# Revit family: Reflex_H_R
name_source: partatom
category: Mechanical Equipment
revit_build: Autodesk Revit 2014 (Build: 20130308_1515(x64)
units: mm (PartAtom-declared; Revit-internal decimal feet)

## types (9) — shared parameters
A1 = 28 mm  [stored 0.0918635 ft]
Angle = 40.00°
Angle1 = 60.00°
Color = gray
Description = Membrane pressure expansion vessel
ETIM Article Class = EC010958
ETIM Name = Membrane pressure expansion vessel
IFCExportAs = ifcexpansion
IFCExportType = EXPANSION
Manufacturer = Reflex
Model = Storatherm Heat H…/R
Reflex_item_color = Color RGB 128-128-128
Revision = 2016
URL = http://reflex.cadprofi.com
V_cov = No

## per-type parameters (varying)
- Reflex H 300/R: A=48.3 mm  [stored 0.158465 ft]; Ang2=0.00°; Art. No.=7783600; Connection=9*Rp 1 1/2; D=597 mm; DL=279.5 mm; DN=40 mm; F=142 mm; H=1320 mm; H1=42 mm; H2=1178 mm; H4=149.25 mm; HC1=225 mm; HC2=490 mm; HC3=760 mm; HC4=1033 mm; HC5=210 mm; HC6=380 mm; HC7=670 mm; HC8=960 mm; HL=750 mm; HRev=265 mm  [stored 0.869423 ft]; HT=0 mm  [stored 0 ft]; LM=398.5 mm; PN=3 bar; RLG=260 mm; RN=520 mm; RT=0 mm  [stored 0 ft]; Scale=1 mm  [stored 0.00328084 ft]; VCon=No; VLeg_b=No; VLeg_m=No; VLeg_s=Yes; VTrans=No; Volume=300.0 L
- Reflex H 500/R: A=48.3 mm  [stored 0.158465 ft]; Ang2=0.00°; Art. No.=7783800; Connection=9*Rp 1 1/2; D=597 mm; DL=279.5 mm; DN=40 mm; F=142 mm; H=1950 mm; H1=42 mm; H2=1808 mm; H4=149.25 mm; HC1=225 mm; HC2=701 mm; HC3=1181 mm; HC4=1655 mm; HC5=210 mm; HC6=375 mm  [stored 1.23031 ft]; HC7=945 mm; HC8=1515 mm; HL=1102 mm; HRev=265 mm  [stored 0.869423 ft]; HT=0 mm  [stored 0 ft]; LM=398.5 mm; PN=3 bar; RLG=260 mm; RN=520 mm; RT=0 mm  [stored 0 ft]; Scale=1 mm  [stored 0.00328084 ft]; VCon=No; VLeg_b=No; VLeg_m=No; VLeg_s=Yes; VTrans=No; Volume=500.0 L
- Reflex H 800/R: A=48.3 mm  [stored 0.158465 ft]; Ang2=0.00°; Art. No.=7784005; Connection=9*Rp 1 1/2; D=790 mm; DL=376 mm; DN=40 mm; F=140 mm; H=1825 mm; H1=40 mm  [stored 0.131234 ft]; H2=1685 mm; H4=197.5 mm  [stored 0.647966 ft]; HC1=236 mm; HC2=656 mm; HC3=1076 mm; HC4=1496 mm; HC5=221 mm; HC6=386 mm  [stored 1.2664 ft]; HC7=896 mm; HC8=1446 mm; HL=1350 mm; HRev=311 mm; HT=0 mm  [stored 0 ft]; LM=495 mm; PN=3 bar; RLG=345.5 mm  [stored 1.13353 ft]; RN=691 mm; RT=0 mm  [stored 0 ft]; Scale=1 mm  [stored 0.00328084 ft]; VCon=No; VLeg_b=No; VLeg_m=Yes; VLeg_s=No; VTrans=No; Volume=800.0 L
- Reflex H 1000/R: A=48.3 mm  [stored 0.158465 ft]; Ang2=0.00°; Art. No.=7784205; Connection=9*Rp 1 1/2; D=790 mm; DL=366.5 mm; DN=40 mm; F=180 mm  [stored 0.590551 ft]; H=2115 mm; H1=80 mm  [stored 0.262467 ft]; H2=1898 mm; H4=197.5 mm  [stored 0.647966 ft]; HC1=310 mm  [stored 1.01706 ft]; HC2=768 mm; HC3=1228 mm; HC4=1681 mm; HC5=296 mm  [stored 0.971129 ft]; HC6=461 mm; HC7=1011 mm; HC8=1581 mm; HL=1320 mm; HRev=386 mm  [stored 1.2664 ft]; HT=0 mm  [stored 0 ft]; LM=495 mm; PN=3 bar; RLG=345.5 mm  [stored 1.13353 ft]; RN=691 mm; RT=0 mm  [stored 0 ft]; Scale=1.5 mm  [stored 0.00492126 ft]; VCon=No; VLeg_b=No; VLeg_m=Yes; VLeg_s=No; VTrans=No; Volume=1000.0 L
- Reflex H 1500/R: A=48.3 mm  [stored 0.158465 ft]; Ang2=0.00°; Art. No.=7784400; Connection=9*Rp 1 1/2; D=1000 mm; DL=471.5 mm; DN=40 mm; F=146 mm; H=2120 mm; H1=46 mm; H2=1974 mm; H4=250 mm; HC1=341 mm; HC2=798 mm; HC3=1258 mm; HC4=1716 mm; HC5=341 mm; HC6=551 mm; HC7=1096 mm; HC8=1566 mm; HL=1250 mm; HRev=421 mm; HT=0 mm  [stored 0 ft]; LM=600 mm; PN=6 bar; RLG=437.5 mm; RN=875 mm; RT=0 mm  [stored 0 ft]; Scale=1.5 mm  [stored 0.00492126 ft]; VCon=No; VLeg_b=No; VLeg_m=Yes; VLeg_s=No; VTrans=No; Volume=1500.0 L
- Reflex H 2000/R: A=48.3 mm  [stored 0.158465 ft]; Ang2=0.00°; Art. No.=7784600; Connection=9*Rp 1 1/2; D=1200 mm; DL=571.5 mm; DN=40 mm; F=132 mm; H=2122 mm; H1=32 mm; H2=1990 mm; H4=300 mm; HC1=365 mm; HC2=805 mm; HC3=1245 mm; HC4=1680 mm; HC5=365 mm; HC6=575 mm; HC7=1100 mm; HC8=1630 mm; HL=1500 mm; HRev=421 mm; HT=0 mm  [stored 0 ft]; LM=700 mm; PN=6 bar; RLG=510 mm; RN=1020 mm; RT=0 mm  [stored 0 ft]; Scale=1.5 mm  [stored 0.00492126 ft]; VCon=No; VLeg_b=No; VLeg_m=Yes; VLeg_s=No; VTrans=No; Volume=2000.0 L
- Reflex H 3000/R: A=60.3 mm; Ang2=30.00°; Art. No.=7788200; Connection=9*Rp 2; D=1500 mm; DL=721.5 mm; DN=40 mm; F=191 mm; H=2101 mm; H1=91 mm; H2=1910 mm; H4=375 mm  [stored 1.23031 ft]; HC1=495 mm; HC2=845 mm; HC3=1247 mm; HC4=1597 mm; HC5=495 mm; HC6=845 mm; HC7=1247 mm; HC8=1597 mm; HL=1500 mm; HRev=550 mm; HT=1840 mm; LM=850 mm; PN=6 bar; RLG=550 mm; RN=1100 mm; RT=1320 mm; Scale=1.5 mm  [stored 0.00492126 ft]; VCon=Yes; VLeg_b=Yes; VLeg_m=No; VLeg_s=No; VTrans=Yes; Volume=3000.0 L
- Reflex H 4000/R: A=60.3 mm; Ang2=30.00°; Art. No.=7788500; Connection=9*Rp 2; D=1500 mm; DL=721.5 mm; DN=40 mm; F=191 mm; H=2676 mm; H1=91 mm; H2=2485 mm; H4=375 mm  [stored 1.23031 ft]; HC1=496 mm; HC2=1090 mm; HC3=1577 mm; HC4=2171 mm; HC5=496 mm; HC6=1090 mm; HC7=1577 mm; HC8=2171 mm; HL=1500 mm; HRev=550 mm; HT=2420 mm; LM=850 mm; PN=6 bar; RLG=550 mm; RN=1100 mm; RT=1320 mm; Scale=1.5 mm  [stored 0.00492126 ft]; VCon=Yes; VLeg_b=Yes; VLeg_m=No; VLeg_s=No; VTrans=Yes; Volume=4000.0 L
- Reflex H 5000/R: A=60.3 mm; Ang2=30.00°; Art. No.=7788800; Connection=9*Rp 2; D=1500 mm; DL=721.5 mm; DN=50 mm; F=191 mm; H=3211 mm; H1=91 mm; H2=3020 mm; H4=375 mm  [stored 1.23031 ft]; HC1=520 mm; HC2=1305 mm; HC3=1895 mm; HC4=2682 mm; HC5=520 mm; HC6=1305 mm; HC7=1895 mm; HC8=2682 mm; HL=1500 mm; HRev=575 mm; HT=2950 mm; LM=850 mm; PN=6 bar; RLG=550 mm; RN=1100 mm; RT=1320 mm; Scale=1.5 mm  [stored 0.00492126 ft]; VCon=Yes; VLeg_b=Yes; VLeg_m=No; VLeg_s=No; VTrans=Yes; Volume=5000.0 L

note: [stored X ft] marks values corroborated as IEEE doubles in the binary element streams (Revit-internal decimal feet)

## geometry (parser evidence)
native form markers: Extrusion x1, Sweep x16
no freeform markers — native parametric forms only
